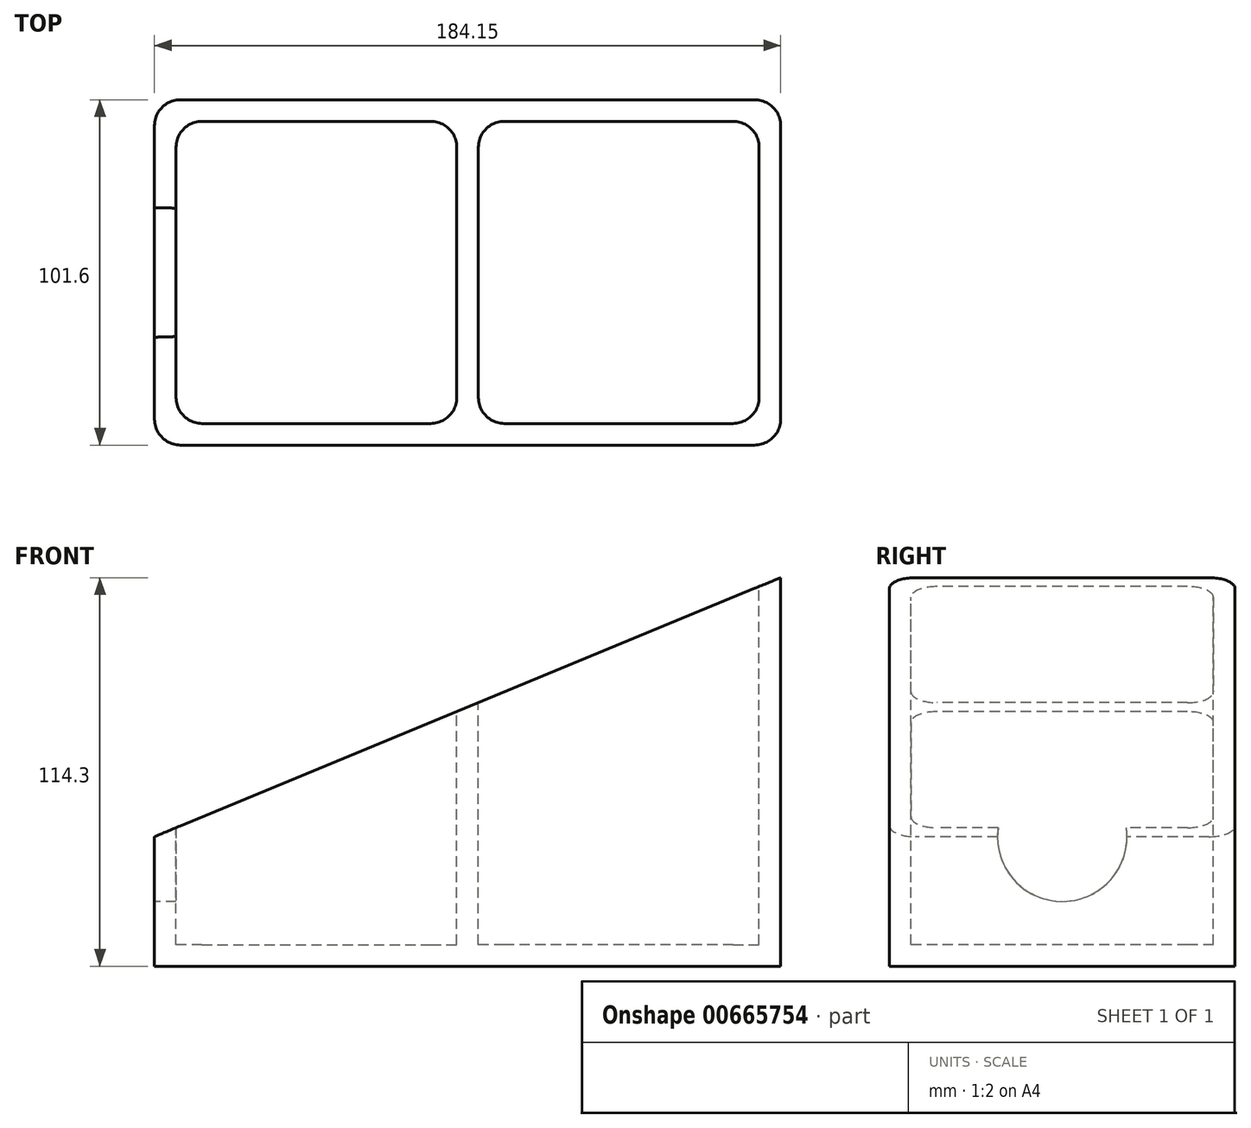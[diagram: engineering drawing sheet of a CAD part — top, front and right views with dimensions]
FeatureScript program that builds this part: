
annotation { "Feature Type Name" : "Feature", "Feature Type Description" : "" }
export const myFeature = defineFeature(function(context is Context, id is Id, definition is map)
    precondition{}
    {
        {
            var Q0;
            Q0=qCreatedBy(makeId("Top.planeOp"),FACE);
            var sketch = newSketch(context, id + "F0", { "sketchPlane" : qUnion([Q0])});
            skLineSegment(sketch, "E0.bottom", {"start": v(-97.37, 42.98) * mm, "end": v(86.78, 42.98) * mm});
            skLineSegment(sketch, "E0.top", {"start": v(-97.37, -58.62) * mm, "end": v(86.78, -58.62) * mm});
            skLineSegment(sketch, "E0.left", {"start": v(-97.37, 42.98) * mm, "end": v(-97.37, -58.62) * mm});
            skLineSegment(sketch, "E0.right", {"start": v(86.78, 42.98) * mm, "end": v(86.78, -58.62) * mm});
            skSolve(sketch);
        }
        {
            var Q0;
            Q0=makeQuery(id+"F0.imprint","IMPRINT",FACE,{"disambiguationData":[TD([[makeQuery(id+"F0.imprint","IMPRINT",EDGE,{"derivedFrom":sQuery(id+"F0.wireOp",EDGE,"E0.bottom")}),-1.0]])]});
            extrude(context, id + "F1", {"entities" : qUnion([Q0]), "depth" : 114.3 * mm, "offsetDistance" : 25.4 * mm});
        }
        {
            var Q0;
            Q0=makeQuery(id+"F1.opExtrude","CAP_FACE",FACE,{"disambiguationData":[OSD([sQuery(id+"F0.wireOp",EDGE,"E0.bottom"),sQuery(id+"F0.wireOp",EDGE,"E0.top"),sQuery(id+"F0.wireOp",EDGE,"E0.left"),sQuery(id+"F0.wireOp",EDGE,"E0.right")])],"isStart":false});
            var sketch = newSketch(context, id + "F2", { "sketchPlane" : qUnion([Q0])});
            skLineSegment(sketch, "E1.1", {"start": v(-91.02, 36.63) * mm, "end": v(-91.02, -52.27) * mm});
            skLineSegment(sketch, "E1.3", {"start": v(80.43, 36.63) * mm, "end": v(80.43, -52.27) * mm});
            skLineSegment(sketch, "E2", {"start": v(-91.02, 36.63) * mm, "end": v(-8.47, 36.63) * mm});
            skLineSegment(sketch, "E3", {"start": v(-8.47, 36.63) * mm, "end": v(-8.47, -52.27) * mm});
            skLineSegment(sketch, "E4", {"start": v(-8.47, -52.27) * mm, "end": v(-91.02, -52.27) * mm});
            skLineSegment(sketch, "E5", {"start": v(80.43, 36.63) * mm, "end": v(-2.12, 36.63) * mm});
            skLineSegment(sketch, "E6", {"start": v(-2.12, 36.63) * mm, "end": v(-2.12, -52.27) * mm});
            skLineSegment(sketch, "E7", {"start": v(-2.12, -52.27) * mm, "end": v(80.43, -52.27) * mm});
            skSolve(sketch);
        }
        {
            var Q0;
            Q0 = qSketchRegion(id + "F2", true);
            extrude(context, id + "F3", {"entities" : qUnion([Q0]), "operationType" : NewBodyOperationType.REMOVE, "oppositeDirection" : true, "depth" : 107.95 * mm, "offsetDistance" : 25.4 * mm});
        }
        {
            var Q0;
            Q0=makeQuery(id+"F1.opExtrude","SWEPT_FACE",FACE,{"disambiguationData":[OSD([sQuery(id+"F0.wireOp",EDGE,"E0.top")])]});
            var sketch = newSketch(context, id + "F4", { "sketchPlane" : qUnion([Q0])});
            skLineSegment(sketch, "E8", {"start": v(-97.37, 38.1) * mm, "end": v(86.78, 114.3) * mm});
            skLineSegment(sketch, "E9", {"start": v(86.78, 114.3) * mm, "end": v(-97.37, 114.3) * mm});
            skLineSegment(sketch, "E10", {"start": v(-97.37, 114.3) * mm, "end": v(-97.37, 38.1) * mm});
            skSolve(sketch);
        }
        {
            var Q0;
            Q0 = qSketchRegion(id + "F4", true);
            extrude(context, id + "F5", {"entities" : qUnion([Q0]), "operationType" : NewBodyOperationType.REMOVE, "endBound" : BoundingType.THROUGH_ALL, "oppositeDirection" : true, "depth" : 25.4 * mm, "offsetDistance" : 25.4 * mm});
        }
        {
            var Q0;
            Q0=makeQuery(id+"F3.boolean.opBoolean","COPY",EDGE,{"derivedFrom":makeQuery(id+"F3.opExtrude","SWEPT_EDGE",EDGE,{"disambiguationData":[OSD([sQuery(id+"F2.wireOp",EDGE,"E1.3"),sQuery(id+"F2.wireOp",EDGE,"E5")])]})});
            var Q1;
            Q1=makeQuery(id+"F3.boolean.opBoolean","COPY",EDGE,{"derivedFrom":makeQuery(id+"F3.opExtrude","SWEPT_EDGE",EDGE,{"disambiguationData":[OSD([sQuery(id+"F2.wireOp",EDGE,"E2"),sQuery(id+"F2.wireOp",EDGE,"E3")])]})});
            var Q2;
            Q2=makeQuery(id+"F1.opExtrude","SWEPT_EDGE",EDGE,{"disambiguationData":[OSD([sQuery(id+"F0.wireOp",EDGE,"E0.bottom"),sQuery(id+"F0.wireOp",EDGE,"E0.left")])]});
            var Q3;
            Q3=makeQuery(id+"F1.opExtrude","SWEPT_EDGE",EDGE,{"disambiguationData":[OSD([sQuery(id+"F0.wireOp",EDGE,"E0.top"),sQuery(id+"F0.wireOp",EDGE,"E0.left")])]});
            var Q4;
            Q4=makeQuery(id+"F1.opExtrude","SWEPT_EDGE",EDGE,{"disambiguationData":[OSD([sQuery(id+"F0.wireOp",EDGE,"E0.top"),sQuery(id+"F0.wireOp",EDGE,"E0.right")])]});
            var Q5;
            Q5=makeQuery(id+"F3.boolean.opBoolean","COPY",EDGE,{"derivedFrom":makeQuery(id+"F3.opExtrude","SWEPT_EDGE",EDGE,{"disambiguationData":[OSD([sQuery(id+"F2.wireOp",EDGE,"E1.3"),sQuery(id+"F2.wireOp",EDGE,"E7")])]})});
            var Q6;
            Q6=makeQuery(id+"F3.boolean.opBoolean","COPY",EDGE,{"derivedFrom":makeQuery(id+"F3.opExtrude","SWEPT_EDGE",EDGE,{"disambiguationData":[OSD([sQuery(id+"F2.wireOp",EDGE,"E3"),sQuery(id+"F2.wireOp",EDGE,"E4")])]})});
            var Q7;
            Q7=makeQuery(id+"F1.opExtrude","SWEPT_EDGE",EDGE,{"disambiguationData":[OSD([sQuery(id+"F0.wireOp",EDGE,"E0.bottom"),sQuery(id+"F0.wireOp",EDGE,"E0.right")])]});
            var Q8;
            Q8=makeQuery(id+"F3.boolean.opBoolean","COPY",EDGE,{"derivedFrom":makeQuery(id+"F3.opExtrude","SWEPT_EDGE",EDGE,{"disambiguationData":[OSD([sQuery(id+"F2.wireOp",EDGE,"E6"),sQuery(id+"F2.wireOp",EDGE,"E7")])]})});
            var Q9;
            Q9=makeQuery(id+"F3.boolean.opBoolean","COPY",EDGE,{"derivedFrom":makeQuery(id+"F3.opExtrude","SWEPT_EDGE",EDGE,{"disambiguationData":[OSD([sQuery(id+"F2.wireOp",EDGE,"E1.1"),sQuery(id+"F2.wireOp",EDGE,"E4")])]})});
            var Q10;
            Q10=makeQuery(id+"F3.boolean.opBoolean","COPY",EDGE,{"derivedFrom":makeQuery(id+"F3.opExtrude","SWEPT_EDGE",EDGE,{"disambiguationData":[OSD([sQuery(id+"F2.wireOp",EDGE,"E5"),sQuery(id+"F2.wireOp",EDGE,"E6")])]})});
            var Q11;
            Q11=makeQuery(id+"F3.boolean.opBoolean","COPY",EDGE,{"derivedFrom":makeQuery(id+"F3.opExtrude","SWEPT_EDGE",EDGE,{"disambiguationData":[OSD([sQuery(id+"F2.wireOp",EDGE,"E1.1"),sQuery(id+"F2.wireOp",EDGE,"E2")])]})});
            fillet(context, id + "F6", {"entities" : qUnion([Q0, Q1, Q2, Q3, Q4, Q5, Q6, Q7, Q8, Q9, Q10, Q11]), "radius" : 7.62 * mm, "tangentPropagation" : true, "allowEdgeOverflow" : false});
        }
        {
            var Q0;
            Q0=makeQuery(id+"F1.opExtrude","SWEPT_FACE",FACE,{"disambiguationData":[OSD([sQuery(id+"F0.wireOp",EDGE,"E0.left")])]});
            var sketch = newSketch(context, id + "F7", { "sketchPlane" : qUnion([Q0])});
            skCircle(sketch, "E11", {"center": v(7.82, 38.1) * mm, "radius": 19.05 * mm});
            skSolve(sketch);
        }
        {
            var Q0;
            Q0 = qSketchRegion(id + "F7", true);
            extrude(context, id + "F8", {"entities" : qUnion([Q0]), "operationType" : NewBodyOperationType.REMOVE, "oppositeDirection" : true, "depth" : 25.4 * mm, "offsetDistance" : 25.4 * mm});
        }
    });
